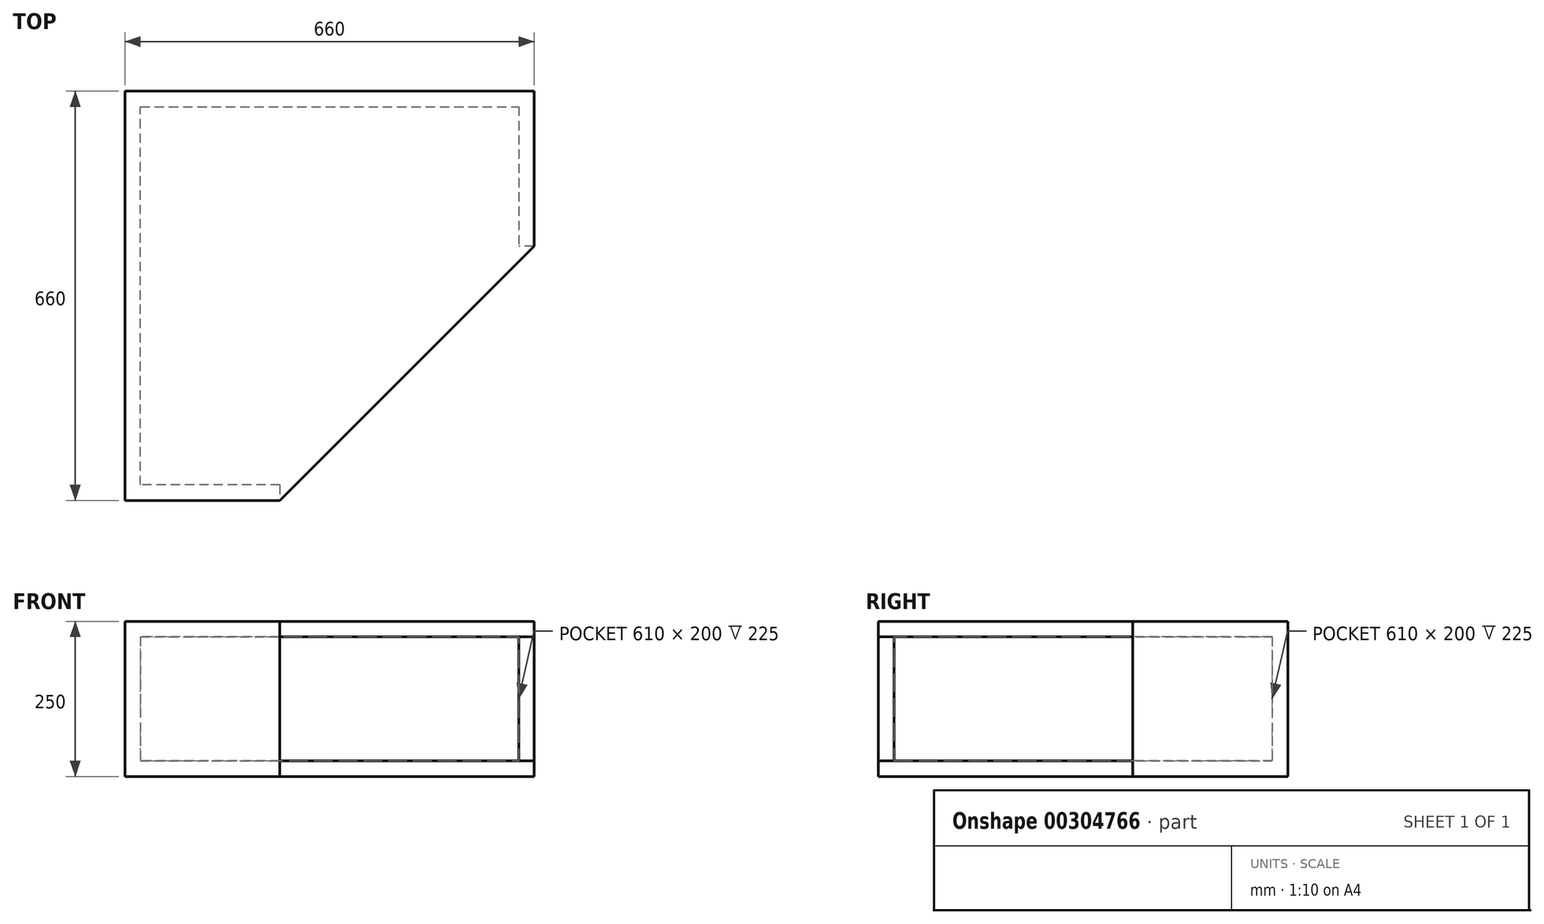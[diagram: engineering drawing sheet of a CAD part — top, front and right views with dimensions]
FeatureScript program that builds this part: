
annotation { "Feature Type Name" : "Feature", "Feature Type Description" : "" }
export const myFeature = defineFeature(function(context is Context, id is Id, definition is map)
    precondition{}
    {
        {
            var Q0;
            Q0=qCreatedBy(makeId("Top.planeOp"),FACE);
            var sketch = newSketch(context, id + "F0", { "sketchPlane" : qUnion([Q0])});
            skLineSegment(sketch, "E0", {"start": v(-401.7, -282.4) * mm, "end": v(-401.7, 377.6) * mm});
            skLineSegment(sketch, "E1", {"start": v(-401.7, 377.6) * mm, "end": v(258.3, 377.6) * mm});
            skLineSegment(sketch, "E2", {"start": v(258.3, 377.6) * mm, "end": v(258.3, 127.6) * mm});
            skLineSegment(sketch, "E3", {"start": v(258.3, 127.6) * mm, "end": v(-151.7, -282.4) * mm});
            skLineSegment(sketch, "E4", {"start": v(-151.7, -282.4) * mm, "end": v(-401.7, -282.4) * mm});
            skSolve(sketch);
        }
        {
            var Q0;
            Q0=makeQuery(id+"F0.imprint","IMPRINT",FACE,{"disambiguationData":[TD([[makeQuery(id+"F0.imprint","IMPRINT",EDGE,{"derivedFrom":sQuery(id+"F0.wireOp",EDGE,"E0")}),-1.0]])]});
            extrude(context, id + "F1", {"entities" : qUnion([Q0]), "depth" : 25 * mm});
        }
        {
            var Q0;
            Q0=makeQuery(id+"F1.opExtrude","CAP_FACE",FACE,{"disambiguationData":[OSD([sQuery(id+"F0.wireOp",EDGE,"E0"),sQuery(id+"F0.wireOp",EDGE,"E1"),sQuery(id+"F0.wireOp",EDGE,"E2"),sQuery(id+"F0.wireOp",EDGE,"E3"),sQuery(id+"F0.wireOp",EDGE,"E4")])],"isStart":false});
            var sketch = newSketch(context, id + "F2", { "sketchPlane" : qUnion([Q0])});
            skLineSegment(sketch, "E5.0", {"start": v(-376.7, 352.6) * mm, "end": v(233.3, 352.6) * mm});
            skLineSegment(sketch, "E5.1", {"start": v(-376.7, -257.4) * mm, "end": v(-376.7, 352.6) * mm});
            skLineSegment(sketch, "E5.2", {"start": v(-151.7, -257.4) * mm, "end": v(-376.7, -257.4) * mm});
            skLineSegment(sketch, "E6.0", {"start": v(-151.7, -282.4) * mm, "end": v(-401.7, -282.4) * mm});
            skLineSegment(sketch, "E7.0", {"start": v(-401.7, -282.4) * mm, "end": v(-401.7, 377.6) * mm});
            skLineSegment(sketch, "E8.0", {"start": v(-401.7, 377.6) * mm, "end": v(258.3, 377.6) * mm});
            skLineSegment(sketch, "E9.0", {"start": v(233.3, 352.6) * mm, "end": v(233.3, 127.6) * mm});
            skLineSegment(sketch, "E10", {"start": v(258.3, 377.6) * mm, "end": v(258.3, 127.6) * mm});
            skLineSegment(sketch, "E11", {"start": v(258.3, 127.6) * mm, "end": v(233.3, 127.6) * mm});
            skLineSegment(sketch, "E12", {"start": v(-151.7, -257.4) * mm, "end": v(-151.7, -282.4) * mm});
            skSolve(sketch);
        }
        {
            var Q0;
            Q0=makeQuery(id+"F2.imprint","IMPRINT",FACE,{"disambiguationData":[TD([[makeQuery(id+"F2.imprint","IMPRINT",EDGE,{"derivedFrom":sQuery(id+"F2.wireOp",EDGE,"E5.0")}),1.0]])]});
            extrude(context, id + "F3", {"entities" : qUnion([Q0]), "operationType" : NewBodyOperationType.ADD, "depth" : 200 * mm});
        }
        {
            var Q0;
            Q0=makeQuery(id+"F3.opExtrude","CAP_FACE",FACE,{"disambiguationData":[OSD([sQuery(id+"F2.wireOp",EDGE,"E5.0"),sQuery(id+"F2.wireOp",EDGE,"E5.1"),sQuery(id+"F2.wireOp",EDGE,"E5.2"),sQuery(id+"F2.wireOp",EDGE,"E6.0"),sQuery(id+"F2.wireOp",EDGE,"E7.0"),sQuery(id+"F2.wireOp",EDGE,"E8.0"),sQuery(id+"F2.wireOp",EDGE,"E9.0"),sQuery(id+"F2.wireOp",EDGE,"E10"),sQuery(id+"F2.wireOp",EDGE,"E11"),sQuery(id+"F2.wireOp",EDGE,"E12")])],"isStart":false});
            var sketch = newSketch(context, id + "F4", { "sketchPlane" : qUnion([Q0])});
            skLineSegment(sketch, "E13.0", {"start": v(-151.7, -282.4) * mm, "end": v(-401.7, -282.4) * mm});
            skLineSegment(sketch, "E14.0", {"start": v(-401.7, -282.4) * mm, "end": v(-401.7, 377.6) * mm});
            skLineSegment(sketch, "E15.0", {"start": v(-401.7, 377.6) * mm, "end": v(258.3, 377.6) * mm});
            skLineSegment(sketch, "E16.0", {"start": v(258.3, 377.6) * mm, "end": v(258.3, 127.6) * mm});
            skLineSegment(sketch, "E17.0", {"start": v(258.3, 127.6) * mm, "end": v(-151.7, -282.4) * mm});
            skSolve(sketch);
        }
        {
            var Q0;
            Q0=makeQuery(id+"F4.imprint","IMPRINT",FACE,{"disambiguationData":[TD([[makeQuery(id+"F4.imprint","IMPRINT",EDGE,{"derivedFrom":sQuery(id+"F4.wireOp",EDGE,"E13.0")}),-1.0]])]});
            var Q1;
            Q1=makeQuery(id+"F4.imprint","IMPRINT",FACE,{"disambiguationData":[TD([[makeQuery(id+"F4.imprint","IMPRINT",EDGE,{"derivedFrom":sQuery(id+"F4.wireOp",EDGE,"E17.0")}),-1.0]])]});
            extrude(context, id + "F5", {"entities" : qUnion([Q0, Q1]), "operationType" : NewBodyOperationType.ADD, "depth" : 25 * mm});
        }
    });
